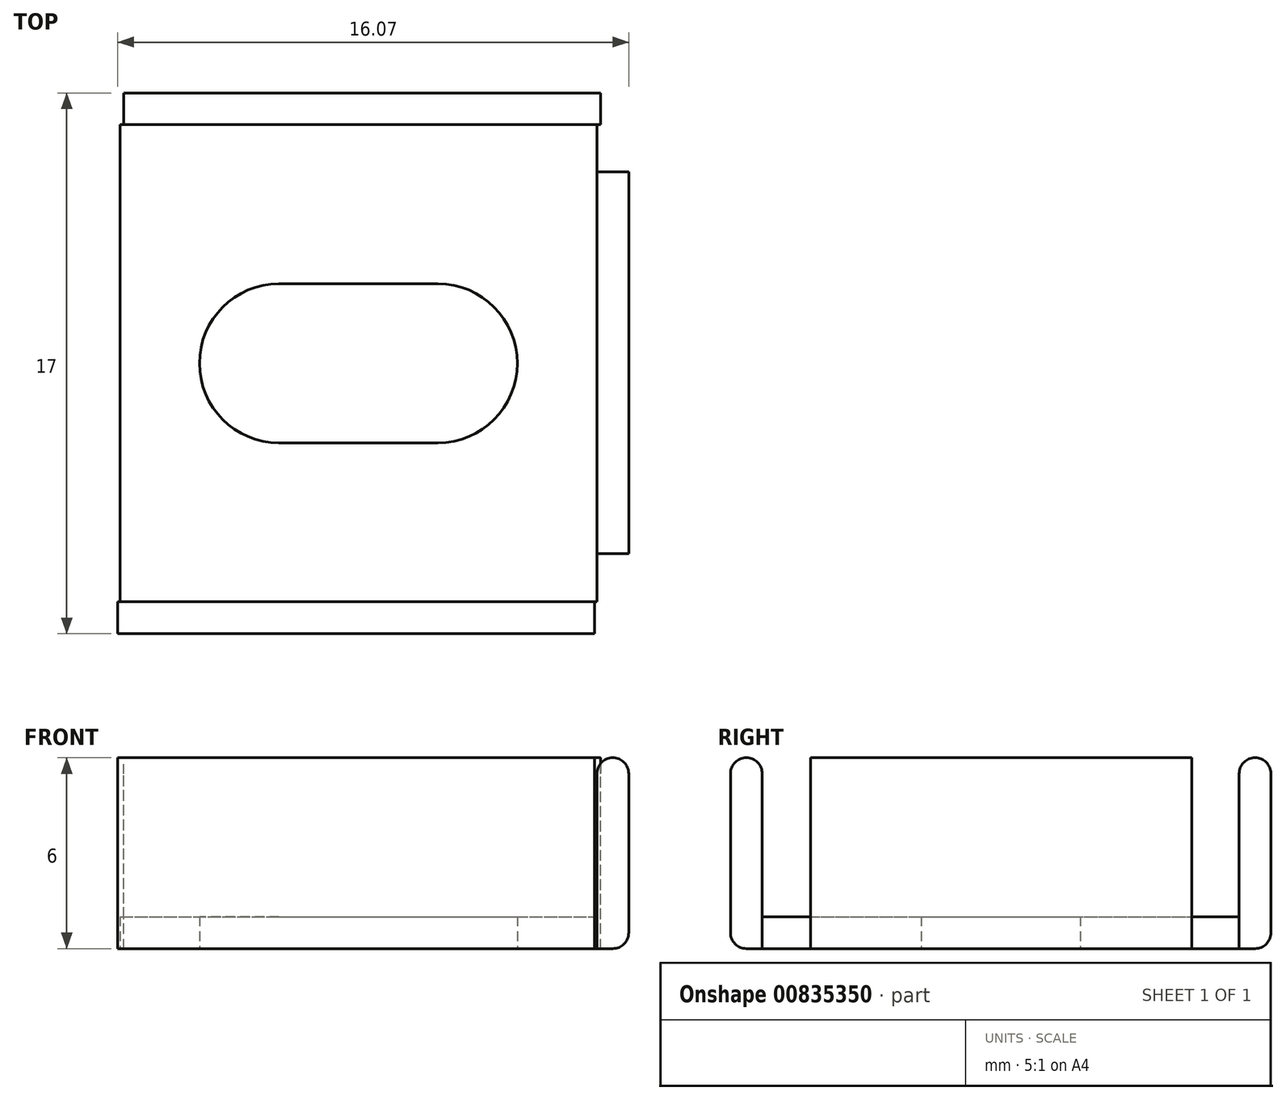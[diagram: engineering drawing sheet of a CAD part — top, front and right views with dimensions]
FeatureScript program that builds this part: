
annotation { "Feature Type Name" : "Feature", "Feature Type Description" : "" }
export const myFeature = defineFeature(function(context is Context, id is Id, definition is map)
    precondition{}
    {
        {
            var Q0;
            Q0=qCreatedBy(makeId("Top.planeOp"),FACE);
            var sketch = newSketch(context, id + "F0", { "sketchPlane" : qUnion([Q0])});
            skLineSegment(sketch, "E0.bottom", {"start": v(-7.5, -7.5) * mm, "end": v(7.5, -7.5) * mm});
            skLineSegment(sketch, "E0.top", {"start": v(-7.5, 7.5) * mm, "end": v(7.5, 7.5) * mm});
            skLineSegment(sketch, "E0.left", {"start": v(-7.5, -7.5) * mm, "end": v(-7.5, 7.5) * mm});
            skLineSegment(sketch, "E0.right", {"start": v(7.5, -7.5) * mm, "end": v(7.5, 7.5) * mm});
            skPoint(sketch, "E0.middle", {"position": v(0, 0) * mm});
            skLineSegment(sketch, "E1.bottom", {"start": v(-2.5, 2.5) * mm, "end": v(2.5, 2.5) * mm});
            skLineSegment(sketch, "E1.top", {"start": v(-2.5, -2.5) * mm, "end": v(2.5, -2.5) * mm});
            skLineSegment(sketch, "E1.left", {"start": v(-5, 0) * mm, "end": v(-5, 0) * mm});
            skLineSegment(sketch, "E1.right", {"start": v(5, 0) * mm, "end": v(5, 0) * mm});
            skPoint(sketch, "E2.visualSharp", {"position": v(5, 2.5) * mm});
            skArc(sketch, "E2.filletArc", {"start": v(5, 0) * mm, "mid": v(4.27, 1.77) * mm, "end": v(2.5, 2.5) * mm});
            skPoint(sketch, "E3.visualSharp", {"position": v(5, -2.5) * mm});
            skArc(sketch, "E3.filletArc", {"start": v(2.5, -2.5) * mm, "mid": v(4.27, -1.77) * mm, "end": v(5, 0) * mm});
            skPoint(sketch, "E4.visualSharp", {"position": v(-5, -2.5) * mm});
            skArc(sketch, "E4.filletArc", {"start": v(-5, 0) * mm, "mid": v(-4.27, -1.77) * mm, "end": v(-2.5, -2.5) * mm});
            skPoint(sketch, "E5.visualSharp", {"position": v(-5, 2.5) * mm});
            skArc(sketch, "E5.filletArc", {"start": v(-2.5, 2.5) * mm, "mid": v(-4.27, 1.77) * mm, "end": v(-5, 0) * mm});
            skSolve(sketch);
        }
        {
            var Q0;
            Q0=sQuery(id+"F0.wireOp",EDGE,"E0.bottom");
            cPoint(context, id + "F1", {"entities" : qUnion([Q0]), "parameter" : 0.5});
        }
        {
            var Q0;
            Q0 = qCreatedBy(id + "F1" ,VERTEX);
            var Q1;
            Q1=qCreatedBy(makeId("Front.planeOp"),FACE);
            cPlane(context, id + "F2", {"entities" : qUnion([Q0, Q1]), "cplaneType" : CPlaneType.PLANE_POINT, "offset" : 25 * mm, "width" : 150 * mm, "height" : 150 * mm});
        }
        {
            var Q0;
            Q0=sQuery(id+"F0.wireOp",EDGE,"E0.top");
            cPoint(context, id + "F3", {"entities" : qUnion([Q0]), "parameter" : 0.5});
        }
        {
            var Q0;
            Q0 = qCreatedBy(id + "F3" ,VERTEX);
            var Q1;
            Q1=qCreatedBy(id+"F2.planeOp",FACE);
            cPlane(context, id + "F4", {"entities" : qUnion([Q0, Q1]), "cplaneType" : CPlaneType.PLANE_POINT, "offset" : 25 * mm, "width" : 150 * mm, "height" : 150 * mm});
        }
        {
            var Q0;
            Q0=sQuery(id+"F0.wireOp",EDGE,"E0.right");
            cPoint(context, id + "F5", {"entities" : qUnion([Q0]), "parameter" : 0.5});
        }
        {
            var Q0;
            Q0 = qCreatedBy(id + "F5" ,VERTEX);
            var Q1;
            Q1=qCreatedBy(makeId("Right.planeOp"),FACE);
            cPlane(context, id + "F6", {"entities" : qUnion([Q0, Q1]), "cplaneType" : CPlaneType.PLANE_POINT, "offset" : 25 * mm, "width" : 150 * mm, "height" : 150 * mm});
        }
        {
            var Q0;
            Q0=qCreatedBy(id+"F2.planeOp",FACE);
            var sketch = newSketch(context, id + "F7", { "sketchPlane" : qUnion([Q0])});
            skLineSegment(sketch, "E6.bottom", {"start": v(-7.57, 0) * mm, "end": v(7.43, 0) * mm});
            skLineSegment(sketch, "E6.top", {"start": v(-7.57, 6) * mm, "end": v(7.43, 6) * mm});
            skLineSegment(sketch, "E6.left", {"start": v(-7.57, 0) * mm, "end": v(-7.57, 6) * mm});
            skLineSegment(sketch, "E6.right", {"start": v(7.43, 0) * mm, "end": v(7.43, 6) * mm});
            skSolve(sketch);
        }
        {
            var Q0;
            Q0=qCreatedBy(id+"F4.planeOp",FACE);
            var sketch = newSketch(context, id + "F8", { "sketchPlane" : qUnion([Q0])});
            skLineSegment(sketch, "E7.bottom", {"start": v(7.61, 0) * mm, "end": v(-7.39, 0) * mm});
            skLineSegment(sketch, "E7.top", {"start": v(7.61, 6) * mm, "end": v(-7.39, 6) * mm});
            skLineSegment(sketch, "E7.left", {"start": v(7.61, 0) * mm, "end": v(7.61, 6) * mm});
            skLineSegment(sketch, "E7.right", {"start": v(-7.39, 0) * mm, "end": v(-7.39, 6) * mm});
            skSolve(sketch);
        }
        {
            var Q0;
            Q0=qCreatedBy(id+"F6.planeOp",FACE);
            var sketch = newSketch(context, id + "F9", { "sketchPlane" : qUnion([Q0])});
            skLineSegment(sketch, "E8.bottom", {"start": v(-5.98, 0) * mm, "end": v(6.02, 0) * mm});
            skLineSegment(sketch, "E8.top", {"start": v(-5.98, 6) * mm, "end": v(6.02, 6) * mm});
            skLineSegment(sketch, "E8.left", {"start": v(-5.98, 0) * mm, "end": v(-5.98, 6) * mm});
            skLineSegment(sketch, "E8.right", {"start": v(6.02, 0) * mm, "end": v(6.02, 6) * mm});
            skLineSegment(sketch, "E9", {"start": v(0.02, 6) * mm, "end": v(0.02, 0) * mm, "construction": true});
            skSolve(sketch);
        }
        {
            var Q0;
            Q0 = qSketchRegion(id + "F9", true);
            extrude(context, id + "F10", {"entities" : qUnion([Q0]), "depth" : 1 * mm, "offsetDistance" : 25 * mm});
        }
        {
            var Q0;
            Q0 = qSketchRegion(id + "F8", true);
            extrude(context, id + "F11", {"entities" : qUnion([Q0]), "operationType" : NewBodyOperationType.ADD, "oppositeDirection" : true, "depth" : 1 * mm, "offsetDistance" : 25 * mm});
        }
        {
            var Q0;
            Q0=makeQuery(id+"F7.imprint","IMPRINT",FACE,{"disambiguationData":[TD([[makeQuery(id+"F7.imprint","IMPRINT",EDGE,{"derivedFrom":sQuery(id+"F7.wireOp",EDGE,"E6.bottom")}),1.0]])]});
            extrude(context, id + "F12", {"entities" : qUnion([Q0]), "depth" : 1 * mm, "offsetDistance" : 25 * mm});
        }
        {
            var Q0;
            Q0=makeQuery(id+"F0.imprint","IMPRINT",FACE,{"disambiguationData":[TD([[makeQuery(id+"F0.imprint","IMPRINT",EDGE,{"derivedFrom":sQuery(id+"F0.wireOp",EDGE,"E0.bottom")}),1.0]])]});
            extrude(context, id + "F13", {"entities" : qUnion([Q0]), "operationType" : NewBodyOperationType.ADD, "depth" : 1 * mm, "offsetDistance" : 25 * mm});
        }
        {
            var Q0;
            Q0=makeQuery(id+"F10.opExtrude","CAP_EDGE",EDGE,{"disambiguationData":[OSD([sQuery(id+"F9.wireOp",EDGE,"E8.top")])],"isStart":false});
            fillet(context, id + "F14", {"entities" : qUnion([Q0]), "radius" : 0.5 * mm, "tangentPropagation" : true, "allowEdgeOverflow" : false});
        }
        {
            var Q0;
            Q0=makeQuery(id+"F10.opExtrude","CAP_EDGE",EDGE,{"disambiguationData":[OSD([sQuery(id+"F9.wireOp",EDGE,"E8.top")])],"isStart":true});
            var Q1;
            Q1=makeQuery(id+"F10.opExtrude","CAP_EDGE",EDGE,{"disambiguationData":[OSD([sQuery(id+"F9.wireOp",EDGE,"E8.bottom")])],"isStart":false});
            var Q2;
            Q2=makeQuery(id+"F12.opExtrude","CAP_EDGE",EDGE,{"disambiguationData":[OSD([sQuery(id+"F7.wireOp",EDGE,"E6.top")])],"isStart":false});
            var Q3;
            Q3=makeQuery(id+"F12.opExtrude","CAP_EDGE",EDGE,{"disambiguationData":[OSD([sQuery(id+"F7.wireOp",EDGE,"E6.top")])],"isStart":true});
            fillet(context, id + "F15", {"entities" : qUnion([Q0, Q1, Q2, Q3]), "radius" : 0.5 * mm, "tangentPropagation" : true, "allowEdgeOverflow" : false});
        }
        {
            var Q0;
            Q0=makeQuery(id+"F12.opExtrude","CAP_EDGE",EDGE,{"disambiguationData":[OSD([sQuery(id+"F7.wireOp",EDGE,"E6.bottom")])],"isStart":false});
            var Q1;
            Q1=makeQuery(id+"F11.opExtrude","CAP_EDGE",EDGE,{"disambiguationData":[OSD([sQuery(id+"F8.wireOp",EDGE,"E7.bottom")])],"isStart":false});
            var Q2;
            Q2=makeQuery(id+"F11.opExtrude","CAP_EDGE",EDGE,{"disambiguationData":[OSD([sQuery(id+"F8.wireOp",EDGE,"E7.top")])],"isStart":false});
            var Q3;
            Q3=makeQuery(id+"F11.opExtrude","CAP_EDGE",EDGE,{"disambiguationData":[OSD([sQuery(id+"F8.wireOp",EDGE,"E7.top")])],"isStart":true});
            fillet(context, id + "F16", {"entities" : qUnion([Q0, Q1, Q2, Q3]), "radius" : 0.5 * mm, "tangentPropagation" : true, "allowEdgeOverflow" : false});
        }
        {
            var Q0;
            Q0=makeQuery(id+"F0.imprint","IMPRINT",FACE,{"disambiguationData":[TD([[makeQuery(id+"F0.imprint","IMPRINT",EDGE,{"derivedFrom":sQuery(id+"F0.wireOp",EDGE,"E1.bottom")}),-1.0]])]});
            extrude(context, id + "F17", {"entities" : qUnion([Q0]), "operationType" : NewBodyOperationType.REMOVE, "depth" : 1 * mm, "offsetDistance" : 25 * mm});
        }
    });
